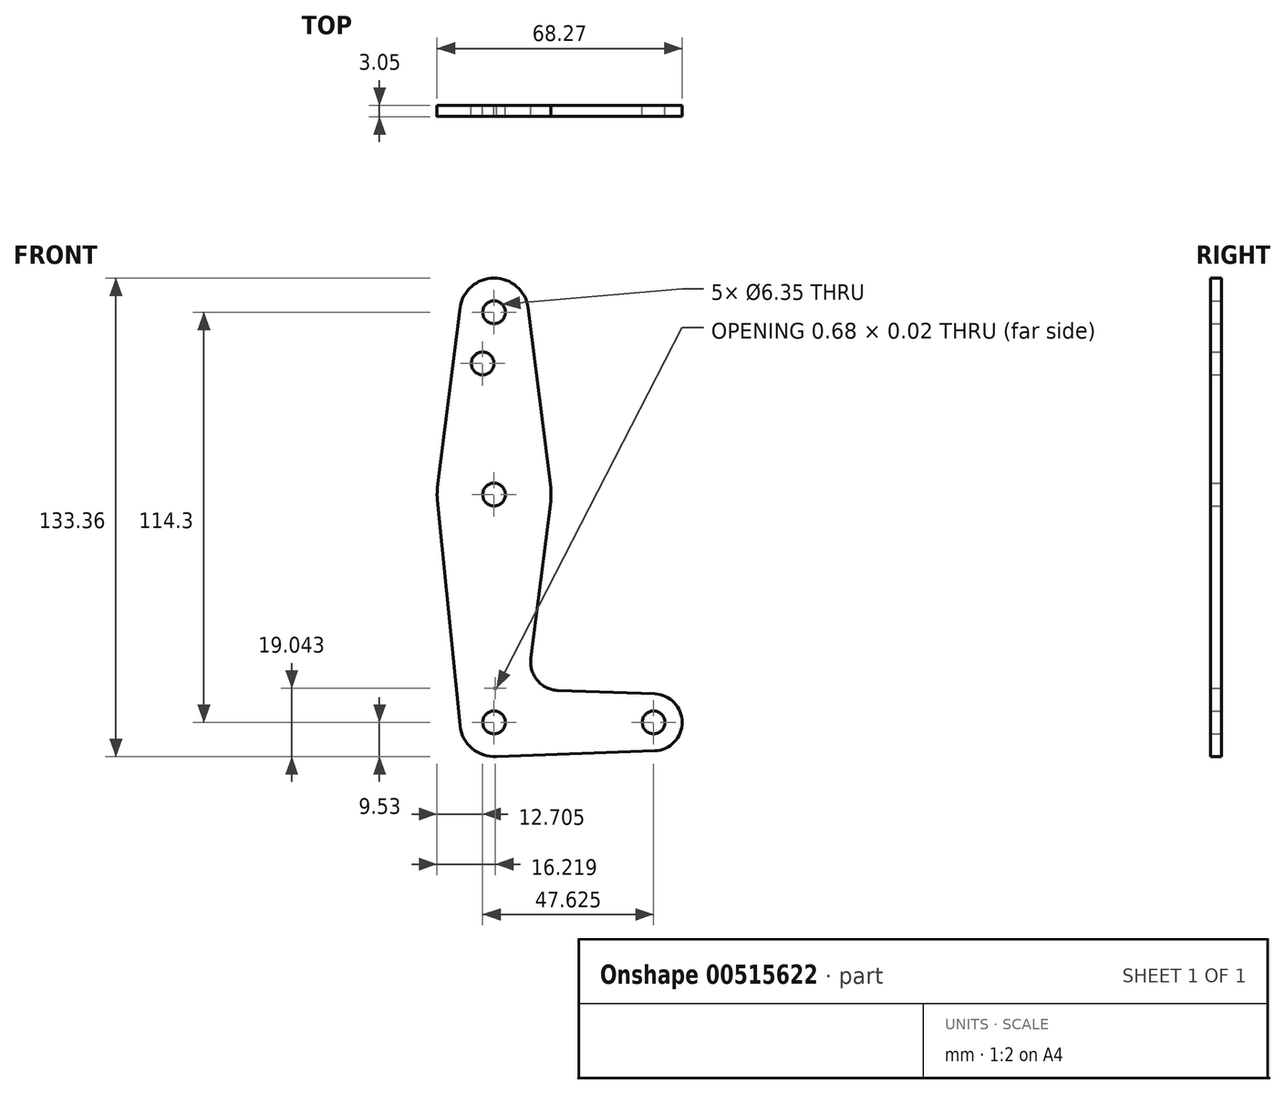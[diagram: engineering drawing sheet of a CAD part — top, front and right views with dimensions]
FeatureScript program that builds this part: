
annotation { "Feature Type Name" : "Feature", "Feature Type Description" : "" }
export const myFeature = defineFeature(function(context is Context, id is Id, definition is map)
    precondition{}
    {
        {
            var Q0;
            Q0=qCreatedBy(makeId("Front.planeOp"),FACE);
            var sketch = newSketch(context, id + "F0", { "sketchPlane" : qUnion([Q0])});
            skCircle(sketch, "E0", {"center": v(0, 114.3) * mm, "radius": 9.53 * mm});
            skCircle(sketch, "E1", {"center": v(0, 0) * mm, "radius": 9.53 * mm});
            skCircle(sketch, "E2", {"center": v(44.45, 0) * mm, "radius": 7.94 * mm});
            skCircle(sketch, "E3", {"center": v(0, 63.5) * mm, "radius": 15.88 * mm});
            skLineSegment(sketch, "E4", {"start": v(-9.45, 115.5) * mm, "end": v(-15.75, 65.48) * mm});
            skLineSegment(sketch, "E5", {"start": v(9.45, 115.5) * mm, "end": v(15.75, 65.48) * mm});
            skCircle(sketch, "E6", {"center": v(0, 114.3) * mm, "radius": 3.18 * mm});
            skCircle(sketch, "E7", {"center": v(0, 63.5) * mm, "radius": 3.18 * mm});
            skCircle(sketch, "E8", {"center": v(0, 0) * mm, "radius": 3.18 * mm});
            skCircle(sketch, "E9", {"center": v(44.45, 0) * mm, "radius": 3.18 * mm});
            skCircle(sketch, "E10", {"center": v(-3.17, 100.03) * mm, "radius": 3.18 * mm});
            skLineSegment(sketch, "E11", {"start": v(0, 114.3) * mm, "end": v(0, 63.5) * mm, "construction": true});
            skLineSegment(sketch, "E12", {"start": v(0, 0) * mm, "end": v(0, 63.5) * mm, "construction": true});
            skLineSegment(sketch, "E13", {"start": v(0, 0) * mm, "end": v(44.45, 0) * mm, "construction": true});
            skLineSegment(sketch, "E14", {"start": v(-15.8, 61.91) * mm, "end": v(-9.48, -0.95) * mm});
            skLineSegment(sketch, "E15", {"start": v(0, 9.52) * mm, "end": v(0.68, 9.5) * mm});
            skLineSegment(sketch, "E16", {"start": v(0, -9.52) * mm, "end": v(44.73, -7.93) * mm});
            skPoint(sketch, "E17.orphan", {"position": v(44.73, 7.93) * mm});
            skLineSegment(sketch, "E18", {"start": v(15.75, 61.52) * mm, "end": v(10.25, 17.83) * mm});
            skLineSegment(sketch, "E19", {"start": v(17.85, 8.9) * mm, "end": v(44.73, 7.93) * mm});
            skArc(sketch, "E20.filletArc", {"start": v(10.25, 17.83) * mm, "mid": v(12.08, 11.69) * mm, "end": v(17.85, 8.9) * mm});
            skSolve(sketch);
        }
        {
            var Q0;
            Q0 = qSketchRegion(id + "F0", true);
            extrude(context, id + "F1", {"entities" : qUnion([Q0]), "depth" : 3.05 * mm, "offsetDistance" : 25.4 * mm});
        }
    });
